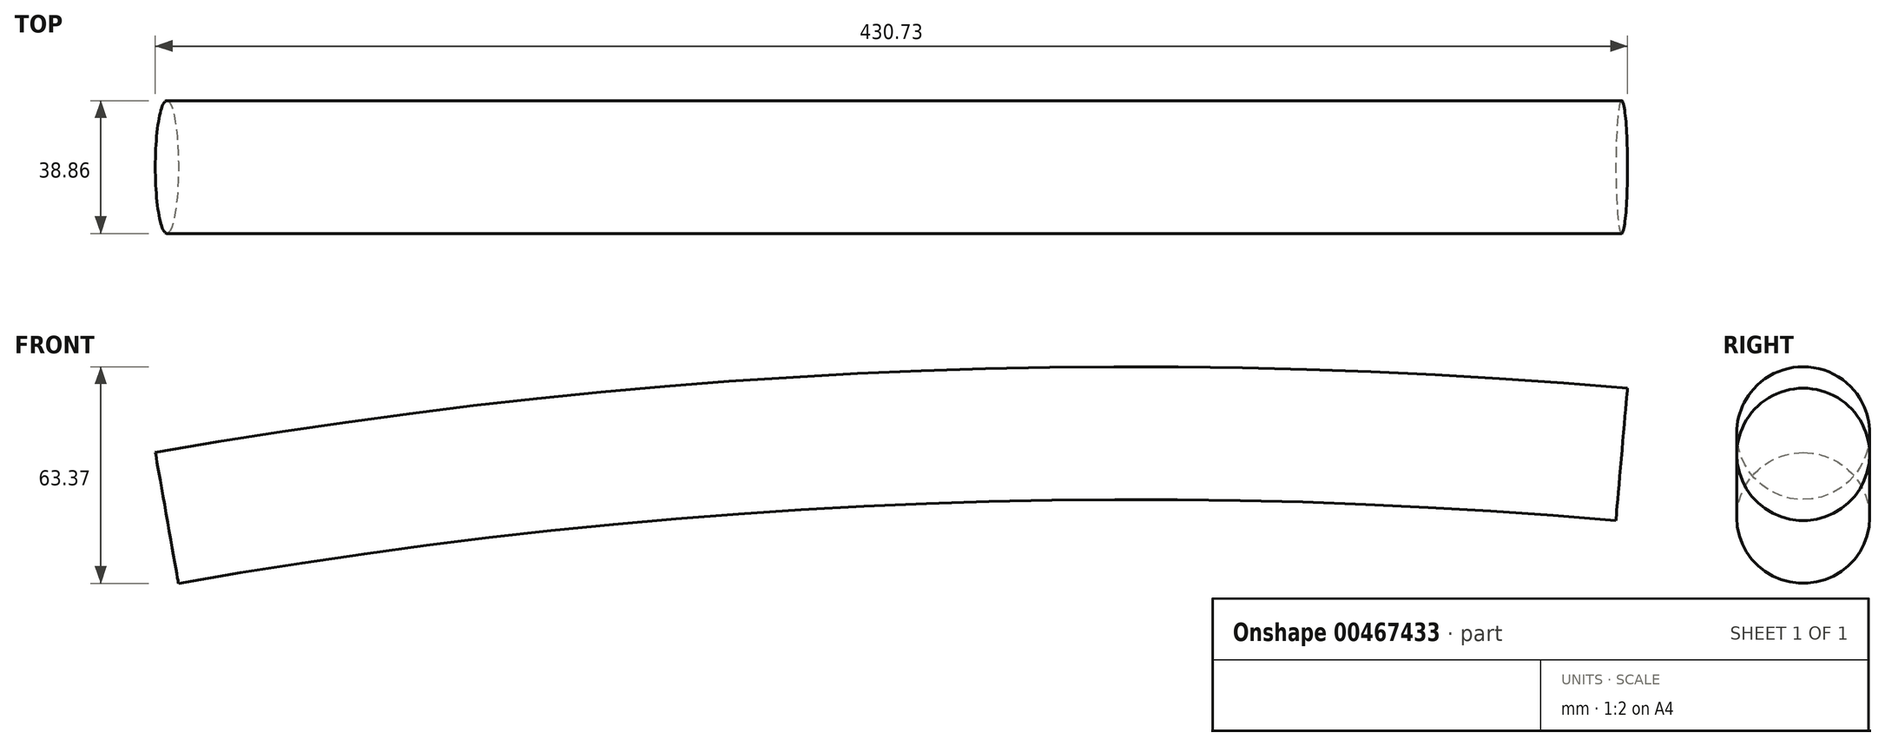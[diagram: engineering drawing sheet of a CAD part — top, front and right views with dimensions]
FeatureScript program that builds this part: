
annotation { "Feature Type Name" : "Feature", "Feature Type Description" : "" }
export const myFeature = defineFeature(function(context is Context, id is Id, definition is map)
    precondition{}
    {
        {
            var Q0;
            Q0=qCreatedBy(makeId("Top.planeOp"),FACE);
            var sketch = newSketch(context, id + "F0", { "sketchPlane" : qUnion([Q0])});
            skLineSegment(sketch, "E0", {"start": v(0, 0) * mm, "end": v(1632.15, 0) * mm});
            skCircle(sketch, "E1", {"center": v(1632.15, 0) * mm, "radius": 19.43 * mm});
            skLineSegment(sketch, "E2", {"start": v(0, 18.17) * mm, "end": v(0, -26.19) * mm});
            skSolve(sketch);
        }
        {
            var Q0;
            Q0=makeQuery(id+"F0.imprint","IMPRINT",FACE,{"disambiguationData":[TD([[makeQuery(id+"F0.imprint","IMPRINT",EDGE,{"derivedFrom":sQuery(id+"F0.wireOp",EDGE,"E1")}),1.0]])]});
            var Q1;
            Q1=sQuery(id+"F0.wireOp",EDGE,"E2");
            revolve(context, id + "F1", {"entities" : qUnion([Q0]), "axis" : qUnion([Q1]), "revolveType" : RevolveType.TWO_DIRECTIONS, "oppositeDirection" : true, "angle" : 275 * degree, "angleBack" : 260 * degree});
        }
    });
